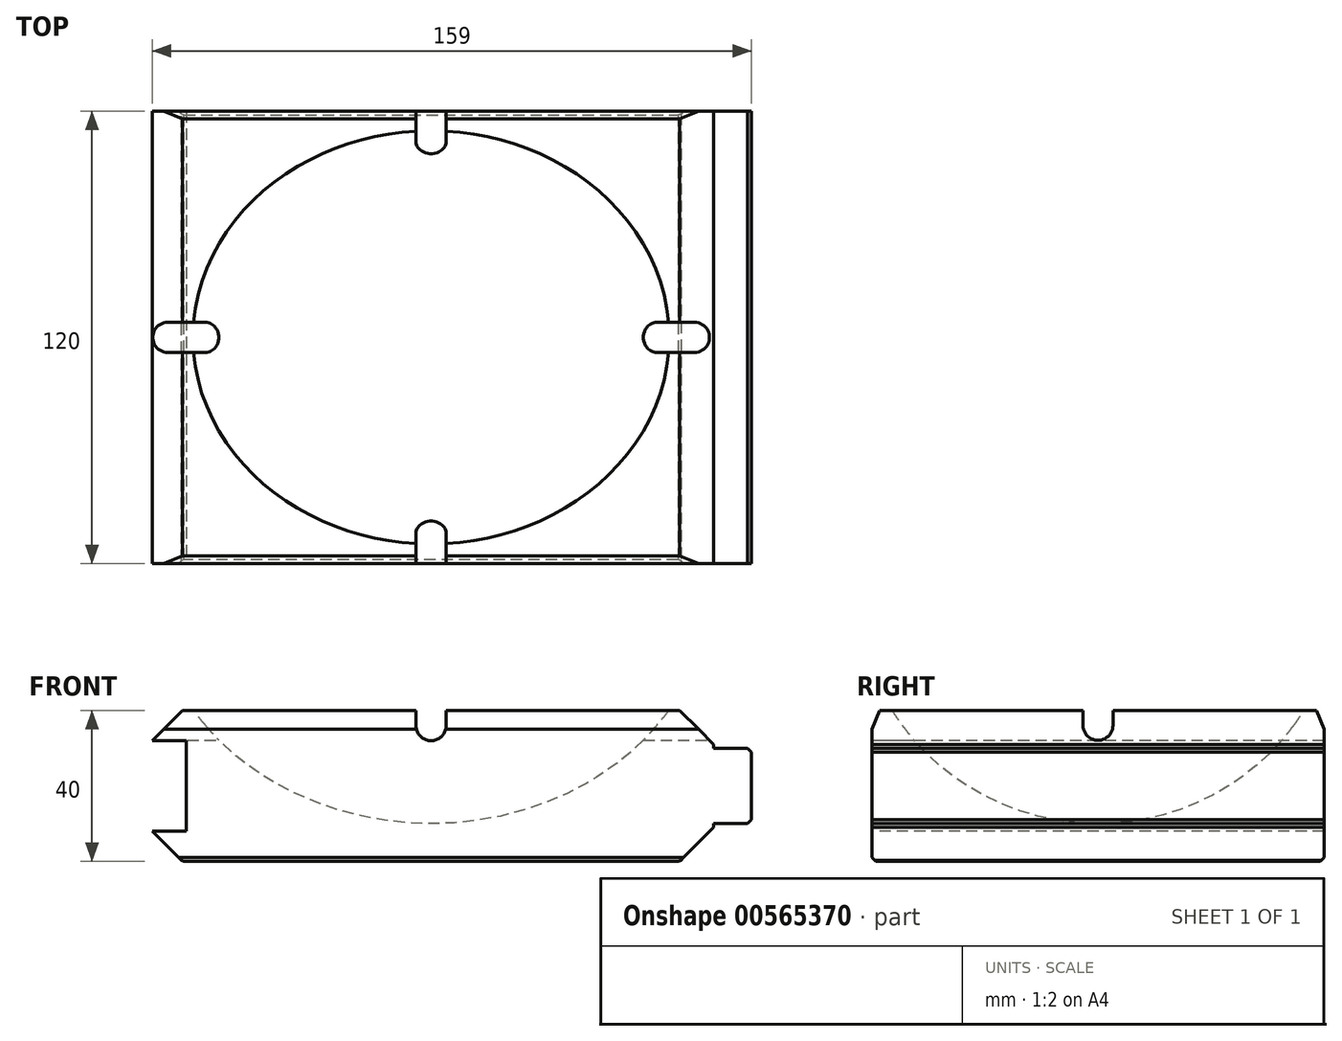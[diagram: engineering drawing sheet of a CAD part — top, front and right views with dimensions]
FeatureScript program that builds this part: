
annotation { "Feature Type Name" : "Feature", "Feature Type Description" : "" }
export const myFeature = defineFeature(function(context is Context, id is Id, definition is map)
    precondition{}
    {
        {
            var Q0;
            Q0=qCreatedBy(makeId("Front.planeOp"),FACE);
            var sketch = newSketch(context, id + "F0", { "sketchPlane" : qUnion([Q0])});
            skLineSegment(sketch, "E0", {"start": v(-75, 0) * mm, "end": v(75, 0) * mm});
            skLineSegment(sketch, "E1", {"start": v(75, 0) * mm, "end": v(75, 10) * mm});
            skLineSegment(sketch, "E2", {"start": v(75, 10) * mm, "end": v(85, 10) * mm});
            skLineSegment(sketch, "E3", {"start": v(85, 10) * mm, "end": v(85, 30) * mm});
            skLineSegment(sketch, "E4", {"start": v(85, 30) * mm, "end": v(75, 30) * mm});
            skLineSegment(sketch, "E5", {"start": v(75, 30) * mm, "end": v(75, 40) * mm});
            skLineSegment(sketch, "E6", {"start": v(75, 40) * mm, "end": v(-75, 40) * mm});
            skLineSegment(sketch, "E7", {"start": v(-75, 40) * mm, "end": v(-75, 32) * mm});
            skLineSegment(sketch, "E8", {"start": v(-75, 32) * mm, "end": v(-65, 32) * mm});
            skLineSegment(sketch, "E9", {"start": v(-65, 32) * mm, "end": v(-65, 8) * mm});
            skLineSegment(sketch, "E10", {"start": v(-65, 8) * mm, "end": v(-75, 8) * mm});
            skLineSegment(sketch, "E11", {"start": v(-75, 8) * mm, "end": v(-75, 0) * mm});
            skSolve(sketch);
        }
        {
            var Q0;
            Q0=makeQuery(id+"F0.imprint","IMPRINT",FACE,{"disambiguationData":[TD([[makeQuery(id+"F0.imprint","IMPRINT",EDGE,{"derivedFrom":sQuery(id+"F0.wireOp",EDGE,"E0")}),1.0]])]});
            extrude(context, id + "F1", {"entities" : qUnion([Q0]), "oppositeDirection" : true, "depth" : 120 * mm, "offsetDistance" : 25 * mm});
        }
        {
            var Q0;
            Q0=makeQuery(id+"F1.opExtrude","CAP_EDGE",EDGE,{"disambiguationData":[OSD([sQuery(id+"F0.wireOp",EDGE,"E6")])],"isStart":true});
            var Q1;
            Q1=makeQuery(id+"F1.opExtrude","CAP_EDGE",EDGE,{"disambiguationData":[OSD([sQuery(id+"F0.wireOp",EDGE,"E6")])],"isStart":false});
            chamfer(context, id + "F2", {"entities" : qUnion([Q0, Q1]), "chamferType" : ChamferType.TWO_OFFSETS, "width1" : 5 * mm, "oppositeDirection" : false, "width2" : 2 * mm, "tangentPropagation" : true});
        }
        {
            var Q0;
            Q0=makeQuery(id+"F1.opExtrude","SWEPT_EDGE",EDGE,{"disambiguationData":[OSD([sQuery(id+"F0.wireOp",EDGE,"E5"),sQuery(id+"F0.wireOp",EDGE,"E6")])]});
            var Q1;
            Q1=makeQuery(id+"F1.opExtrude","SWEPT_EDGE",EDGE,{"disambiguationData":[OSD([sQuery(id+"F0.wireOp",EDGE,"E6"),sQuery(id+"F0.wireOp",EDGE,"E7")])]});
            var Q2;
            Q2=makeQuery(id+"F1.opExtrude","SWEPT_EDGE",EDGE,{"disambiguationData":[OSD([sQuery(id+"F0.wireOp",EDGE,"E0"),sQuery(id+"F0.wireOp",EDGE,"E11")])]});
            var Q3;
            Q3=makeQuery(id+"F1.opExtrude","SWEPT_EDGE",EDGE,{"disambiguationData":[OSD([sQuery(id+"F0.wireOp",EDGE,"E0"),sQuery(id+"F0.wireOp",EDGE,"E1")])]});
            chamfer(context, id + "F3", {"entities" : qUnion([Q0, Q1, Q2, Q3]), "width" : 9 * mm, "tangentPropagation" : true});
        }
        {
            var Q0;
            Q0=makeQuery(id+"F1.opExtrude","SWEPT_EDGE",EDGE,{"disambiguationData":[OSD([sQuery(id+"F0.wireOp",EDGE,"E3"),sQuery(id+"F0.wireOp",EDGE,"E4")])]});
            var Q1;
            Q1=makeQuery(id+"F1.opExtrude","SWEPT_EDGE",EDGE,{"disambiguationData":[OSD([sQuery(id+"F0.wireOp",EDGE,"E2"),sQuery(id+"F0.wireOp",EDGE,"E3")])]});
            var Q2;
            Q2=makeQuery(id+"F1.opExtrude","CAP_EDGE",EDGE,{"disambiguationData":[OSD([sQuery(id+"F0.wireOp",EDGE,"E0")])],"isStart":true});
            var Q3;
            Q3=makeQuery(id+"F1.opExtrude","CAP_EDGE",EDGE,{"disambiguationData":[OSD([sQuery(id+"F0.wireOp",EDGE,"E0")])],"isStart":false});
            var Q4;
            {var subQ0=sQuery(id+"F0.wireOp",EDGE,"E0");Q4=makeQuery(id+"F3.opChamfer","BLEND_EDGE",EDGE,{"blendedFrom":[makeQuery(id+"F1.opExtrude","SWEPT_EDGE",EDGE,{"disambiguationData":[OSD([subQ0,sQuery(id+"F0.wireOp",EDGE,"E11")])]}),makeQuery(id+"F1.opExtrude","SWEPT_FACE",FACE,{"disambiguationData":[OSD([subQ0])]})],"blendedInto":[makeQuery(id+"F1.opExtrude","SWEPT_FACE",FACE,{"disambiguationData":[OSD([subQ0])]})]});}
            var Q5;
            {var subQ0=sQuery(id+"F0.wireOp",EDGE,"E0");Q5=makeQuery(id+"F3.opChamfer","BLEND_EDGE",EDGE,{"blendedFrom":[makeQuery(id+"F1.opExtrude","SWEPT_EDGE",EDGE,{"disambiguationData":[OSD([subQ0,sQuery(id+"F0.wireOp",EDGE,"E1")])]}),makeQuery(id+"F1.opExtrude","SWEPT_FACE",FACE,{"disambiguationData":[OSD([subQ0])]})],"blendedInto":[makeQuery(id+"F1.opExtrude","SWEPT_FACE",FACE,{"disambiguationData":[OSD([subQ0])]})]});}
            chamfer(context, id + "F4", {"entities" : qUnion([Q0, Q1, Q2, Q3, Q4, Q5]), "width" : 1 * mm, "tangentPropagation" : true});
        }
        {
            var Q0;
            Q0=makeQuery(id+"F1.opExtrude","SWEPT_FACE",FACE,{"disambiguationData":[OSD([sQuery(id+"F0.wireOp",EDGE,"E6")])]});
            cPlane(context, id + "F5", {"entities" : qUnion([Q0]), "cplaneType" : CPlaneType.OFFSET, "offset" : 35 * mm, "width" : 150 * mm, "height" : 150 * mm});
        }
        {
            var Q0;
            Q0=qCreatedBy(id+"F5.planeOp",FACE);
            var sketch = newSketch(context, id + "F6", { "sketchPlane" : qUnion([Q0])});
            skEllipticalArc(sketch, "E12", {});
            skLineSegment(sketch, "E13.0", {"start": v(66, 118) * mm, "end": v(-66, 118) * mm, "construction": true});
            skLineSegment(sketch, "E14.0", {"start": v(-66, 2) * mm, "end": v(33.86, 2) * mm, "construction": true});
            skLineSegment(sketch, "E15", {"start": v(-66, 118) * mm, "end": v(66, 2) * mm, "construction": true});
            skLineSegment(sketch, "E16", {"start": v(-75, 60) * mm, "end": v(75, 60) * mm});
            const initialGuessF6  = {"E12": [0, 0.06, 1, 0, 0.075, 0.065, 0, 3.141592653589793]};
            skSetInitialGuess(sketch, initialGuessF6);
            skSolve(sketch);
        }
        {
            var Q0;
            Q0 = qSketchRegion(id + "F6", true);
            var sketch = newSketch(context, id + "F7", { "sketchPlane" : qUnion([Q0])});
            skLineSegment(sketch, "E17", {"start": v(-100.82, 60) * mm, "end": v(99.18, 60) * mm, "construction": true});
            skLineSegment(sketch, "E18.0", {"start": v(66, 118) * mm, "end": v(-66, 118) * mm, "construction": true});
            skLineSegment(sketch, "E19.0", {"start": v(-66, 2) * mm, "end": v(33.86, 2) * mm, "construction": true});
            skSolve(sketch);
        }
        {
            var Q0;
            Q0=makeQuery(id+"F6.imprint","IMPRINT",FACE,{"disambiguationData":[TD([[makeQuery(id+"F6.imprint","IMPRINT",EDGE,{"derivedFrom":sQuery(id+"F6.wireOp",EDGE,"E12")}),1.0]])]});
            var Q1;
            Q1=sQuery(id+"F7.wireOp",EDGE,"E17");
            revolve(context, id + "F8", {"operationType" : NewBodyOperationType.REMOVE, "entities" : qUnion([Q0]), "axis" : qUnion([Q1]), "revolveType" : RevolveType.FULL, "oppositeDirection" : true});
        }
        {
            var Q0;
            Q0=makeQuery(id+"F1.opExtrude","CAP_FACE",FACE,{"disambiguationData":[OSD([sQuery(id+"F0.wireOp",EDGE,"E0"),sQuery(id+"F0.wireOp",EDGE,"E1"),sQuery(id+"F0.wireOp",EDGE,"E2"),sQuery(id+"F0.wireOp",EDGE,"E3"),sQuery(id+"F0.wireOp",EDGE,"E4"),sQuery(id+"F0.wireOp",EDGE,"E5"),sQuery(id+"F0.wireOp",EDGE,"E6"),sQuery(id+"F0.wireOp",EDGE,"E7"),sQuery(id+"F0.wireOp",EDGE,"E8"),sQuery(id+"F0.wireOp",EDGE,"E9"),sQuery(id+"F0.wireOp",EDGE,"E10"),sQuery(id+"F0.wireOp",EDGE,"E11")])],"isStart":true});
            var sketch = newSketch(context, id + "F9", { "sketchPlane" : qUnion([Q0])});
            skPoint(sketch, "E20.0", {"position": v(66, 40) * mm});
            skPoint(sketch, "E21.0", {"position": v(-66, 40) * mm});
            skLineSegment(sketch, "E22", {"start": v(0, -33.24) * mm, "end": v(0, 142.2) * mm, "construction": true});
            skLineSegment(sketch, "E23.0", {"start": v(-66, 40) * mm, "end": v(66, 40) * mm, "construction": true});
            skLineSegment(sketch, "E24", {"start": v(4, 40) * mm, "end": v(4, 36) * mm});
            skLineSegment(sketch, "E25", {"start": v(4, 36) * mm, "end": v(4, 36) * mm});
            skLineSegment(sketch, "E26", {"start": v(-4, 40) * mm, "end": v(-4, 36) * mm});
            skArc(sketch, "E27", {"start": v(4, 36) * mm, "mid": v(0, 32) * mm, "end": v(-4, 36) * mm});
            skLineSegment(sketch, "E28", {"start": v(-4, 40) * mm, "end": v(4, 40) * mm});
            skSolve(sketch);
        }
        {
            var Q0;
            Q0 = qSketchRegion(id + "F9", true);
            extrude(context, id + "F10", {"entities" : qUnion([Q0]), "operationType" : NewBodyOperationType.REMOVE, "endBound" : BoundingType.THROUGH_ALL, "oppositeDirection" : true, "depth" : 25 * mm, "offsetDistance" : 25 * mm});
        }
        {
            var Q0;
            Q0=makeQuery(id+"F1.opExtrude","SWEPT_FACE",FACE,{"disambiguationData":[OSD([sQuery(id+"F0.wireOp",EDGE,"E3")])]});
            var sketch = newSketch(context, id + "F11", { "sketchPlane" : qUnion([Q0])});
            skPoint(sketch, "E29.0", {"position": v(65.56, 1.34) * mm});
            skPoint(sketch, "E30.0", {"position": v(-6, 40) * mm});
            skLineSegment(sketch, "E31", {"start": v(60, -33.94) * mm, "end": v(60, 141.5) * mm, "construction": true});
            skLineSegment(sketch, "E32", {"start": v(64, 40) * mm, "end": v(64, 36.1) * mm});
            skLineSegment(sketch, "E33", {"start": v(64, 36.1) * mm, "end": v(64, 36.1) * mm});
            skLineSegment(sketch, "E34", {"start": v(56, 40) * mm, "end": v(56, 36.1) * mm});
            skArc(sketch, "E35", {"start": v(64, 36.1) * mm, "mid": v(60, 32.1) * mm, "end": v(56, 36.1) * mm});
            skLineSegment(sketch, "E36", {"start": v(56, 40) * mm, "end": v(64, 40) * mm});
            skLineSegment(sketch, "E37.0", {"start": v(2, 40) * mm, "end": v(118, 40) * mm, "construction": true});
            skSolve(sketch);
        }
        {
            var Q0;
            {var subQ5=sQuery(id+"F11.wireOp",EDGE,"E32");Q0=makeQuery(id+"F11.imprint","IMPRINT",FACE,{"disambiguationData":[TD([[makeQuery(id+"F11.imprint","IMPRINT",EDGE,{"derivedFrom":subQ5}),-1.0]])]});}
            extrude(context, id + "F12", {"entities" : qUnion([Q0]), "operationType" : NewBodyOperationType.REMOVE, "endBound" : BoundingType.THROUGH_ALL, "oppositeDirection" : true, "depth" : 25 * mm, "offsetDistance" : 25 * mm});
        }
    });
